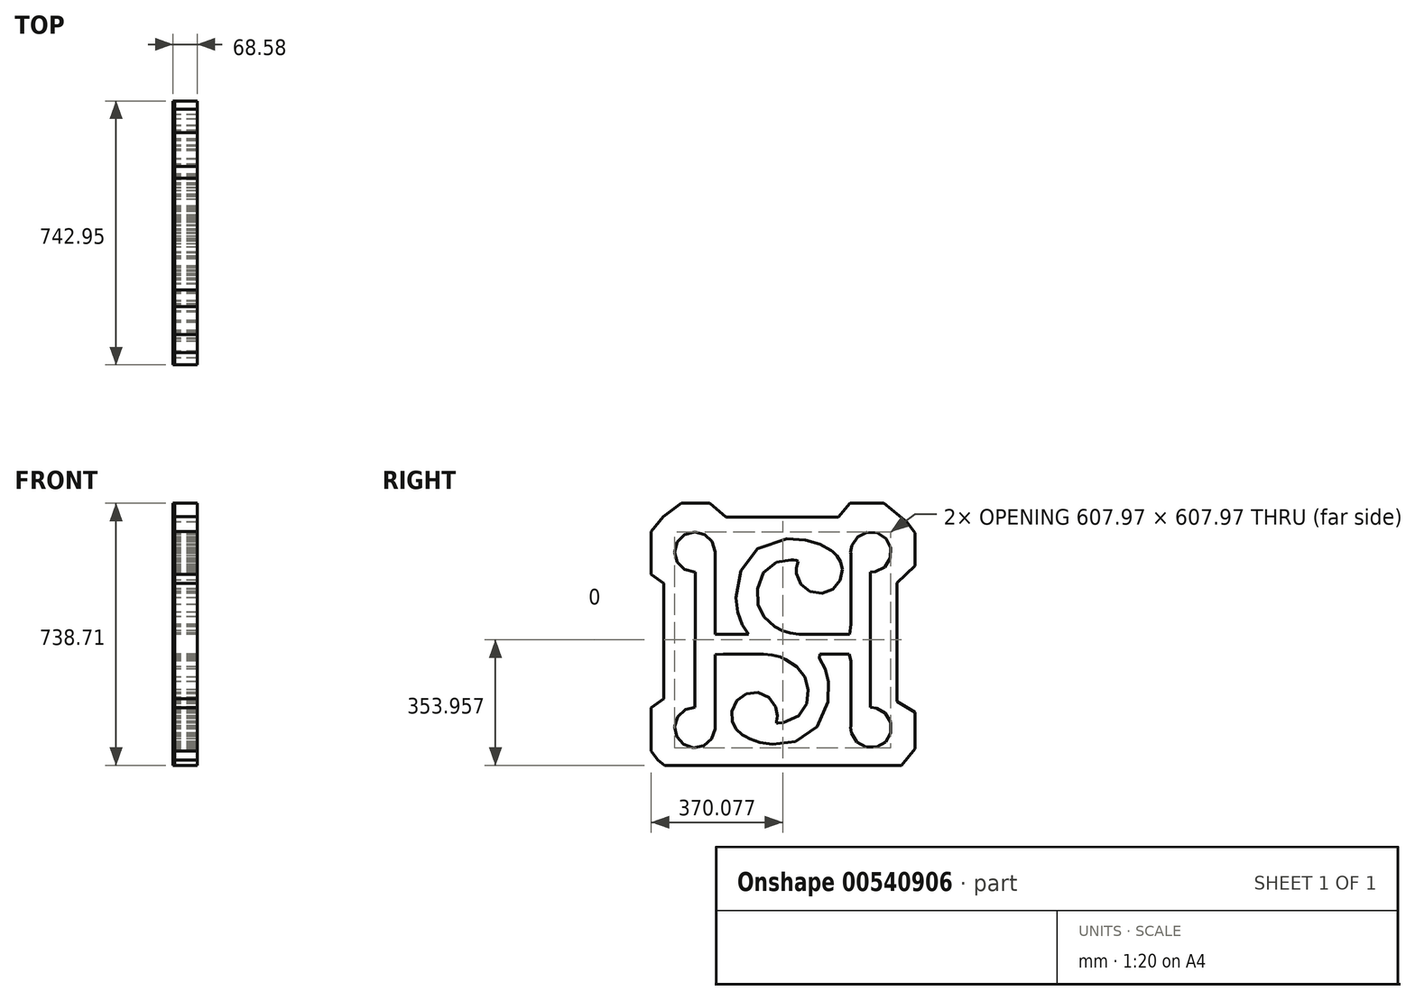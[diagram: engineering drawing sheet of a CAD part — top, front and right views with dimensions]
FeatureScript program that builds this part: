
annotation { "Feature Type Name" : "Feature", "Feature Type Description" : "" }
export const myFeature = defineFeature(function(context is Context, id is Id, definition is map)
    precondition{}
    {
        {
            var Q0;
            Q0=qCreatedBy(makeId("Right.planeOp"),FACE);
            var sketch = newSketch(context, id + "F0", { "sketchPlane" : qUnion([Q0])});
            skFitSpline(sketch, "E0.0", {"points": [v(137.92, 349.27) * mm, v(32.64, 349.27) * mm, v(-72.64, 349.27) * mm, v(-177.92, 349.27) * mm]});
            skFitSpline(sketch, "E1.0", {"points": [v(266.41, 388.54) * mm, v(234.68, 388.54) * mm, v(202.94, 388.54) * mm, v(171.2, 388.54) * mm]});
            skFitSpline(sketch, "E2.0", {"points": [v(171.2, 388.54) * mm, v(160.11, 375.45) * mm, v(149.02, 362.36) * mm, v(137.92, 349.27) * mm]});
            skPoint(sketch, "E3", {"position": v(171.2, 388.54) * mm});
            skFitSpline(sketch, "E4.0", {"points": [v(331.9, 335.96) * mm, v(310.07, 353.48) * mm, v(288.24, 371) * mm, v(266.41, 388.54) * mm]});
            skPoint(sketch, "E5", {"position": v(266.41, 388.54) * mm});
            skPoint(sketch, "E6", {"position": v(-177.92, 349.27) * mm});
            skFitSpline(sketch, "E7.0", {"points": [v(-223.7, 388.54) * mm, v(-250.18, 388.54) * mm, v(-276.66, 388.54) * mm, v(-303.14, 388.54) * mm]});
            skFitSpline(sketch, "E8.0", {"points": [v(-177.92, 349.27) * mm, v(-193.18, 362.36) * mm, v(-208.44, 375.45) * mm, v(-223.7, 388.54) * mm]});
            skPoint(sketch, "E9", {"position": v(-223.7, 388.54) * mm});
            skFitSpline(sketch, "E10.0", {"points": [v(-303.14, 388.54) * mm, v(-320.17, 376.06) * mm, v(-337.2, 363.58) * mm, v(-354.23, 351.1) * mm]});
            skPoint(sketch, "E11", {"position": v(-303.14, 388.54) * mm});
            skFitSpline(sketch, "E12.0", {"points": [v(-354.23, 351.1) * mm, v(-365.59, 336.95) * mm, v(-376.95, 322.8) * mm, v(-388.3, 308.67) * mm]});
            skPoint(sketch, "E13", {"position": v(-354.23, 351.1) * mm});
            skPoint(sketch, "E14", {"position": v(-388.3, 308.67) * mm});
            skFitSpline(sketch, "E15.0", {"points": [v(-388.3, 308.67) * mm, v(-388.3, 268.38) * mm, v(-388.3, 228.1) * mm, v(-388.3, 187.81) * mm]});
            skFitSpline(sketch, "E16.0", {"points": [v(-388.3, 187.81) * mm, v(-376.58, 179.64) * mm, v(-364.86, 171.48) * mm, v(-353.14, 163.31) * mm]});
            skPoint(sketch, "E17", {"position": v(-388.3, 187.81) * mm});
            skPoint(sketch, "E18", {"position": v(-353.14, 163.31) * mm});
            skFitSpline(sketch, "E19.0", {"points": [v(-353.14, -162.05) * mm, v(-364.86, -170.48) * mm, v(-376.58, -178.91) * mm, v(-388.3, -187.34) * mm]});
            skPoint(sketch, "E20", {"position": v(-353.14, -162.05) * mm});
            skPoint(sketch, "E21", {"position": v(-388.3, -187.34) * mm});
            skFitSpline(sketch, "E22.0", {"points": [v(-388.3, -309.2) * mm, v(-382, -317.8) * mm, v(-375.68, -326.42) * mm, v(-369.37, -335.03) * mm]});
            skFitSpline(sketch, "E23.0", {"points": [v(-369.37, -335.03) * mm, v(-363.09, -340.08) * mm, v(-356.8, -345.12) * mm, v(-350.52, -350.17) * mm]});
            skPoint(sketch, "E24", {"position": v(-388.3, -309.2) * mm});
            skPoint(sketch, "E25", {"position": v(-369.37, -335.03) * mm});
            skPoint(sketch, "E26", {"position": v(-350.52, -350.17) * mm});
            skFitSpline(sketch, "E27.0", {"points": [v(-350.52, -350.17) * mm, v(-128.1, -350.17) * mm, v(94.33, -350.17) * mm, v(316.75, -350.17) * mm]});
            skFitSpline(sketch, "E28.0", {"points": [v(316.75, -350.17) * mm, v(329.39, -334.44) * mm, v(342.02, -318.7) * mm, v(354.65, -302.98) * mm]});
            skPoint(sketch, "E29", {"position": v(316.75, -350.17) * mm});
            skLineSegment(sketch, "E30", {"start": v(-353.14, -162.05) * mm, "end": v(-388.3, -187.34) * mm});
            skLineSegment(sketch, "E31", {"start": v(-388.3, -187.34) * mm, "end": v(-388.3, -309.2) * mm});
            skLineSegment(sketch, "E32", {"start": v(-388.3, -309.2) * mm, "end": v(-369.37, -335.03) * mm});
            skLineSegment(sketch, "E33", {"start": v(-369.37, -335.03) * mm, "end": v(-350.52, -350.17) * mm});
            skLineSegment(sketch, "E34", {"start": v(-350.52, -350.17) * mm, "end": v(316.75, -350.17) * mm});
            skLineSegment(sketch, "E35", {"start": v(316.75, -350.17) * mm, "end": v(354.65, -302.98) * mm});
            skLineSegment(sketch, "E36", {"start": v(-353.14, 163.31) * mm, "end": v(-353.14, -162.05) * mm});
            skFitSpline(sketch, "E37.0", {"points": [v(354.65, 304.9) * mm, v(347.06, 315.26) * mm, v(339.48, 325.6) * mm, v(331.9, 335.96) * mm]});
            skFitSpline(sketch, "E38.0", {"points": [v(354.65, 211.87) * mm, v(354.65, 242.88) * mm, v(354.65, 273.9) * mm, v(354.65, 304.9) * mm]});
            skPoint(sketch, "E39", {"position": v(354.65, 304.9) * mm});
            skPoint(sketch, "E40", {"position": v(331.9, 335.96) * mm});
            skFitSpline(sketch, "E41.0", {"points": [v(303.55, 164.27) * mm, v(320.58, 180.14) * mm, v(337.62, 196) * mm, v(354.65, 211.87) * mm]});
            skPoint(sketch, "E42", {"position": v(354.65, 211.87) * mm});
            skFitSpline(sketch, "E43.0", {"points": [v(303.55, -170.62) * mm, v(303.55, -58.99) * mm, v(303.55, 52.64) * mm, v(303.55, 164.27) * mm]});
            skPoint(sketch, "E44", {"position": v(303.55, 164.27) * mm});
            skLineSegment(sketch, "E45", {"start": v(303.55, 164.27) * mm, "end": v(354.65, 211.87) * mm});
            skLineSegment(sketch, "E46", {"start": v(354.65, 211.87) * mm, "end": v(354.65, 304.9) * mm});
            skLineSegment(sketch, "E47", {"start": v(354.65, 304.9) * mm, "end": v(331.9, 335.96) * mm});
            skLineSegment(sketch, "E48", {"start": v(331.9, 335.96) * mm, "end": v(266.41, 388.54) * mm});
            skFitSpline(sketch, "E49.0", {"points": [v(354.65, -200.14) * mm, v(337.62, -190.3) * mm, v(320.58, -180.46) * mm, v(303.55, -170.62) * mm]});
            skFitSpline(sketch, "E50.0", {"points": [v(354.65, -302.98) * mm, v(354.65, -268.7) * mm, v(354.65, -234.42) * mm, v(354.65, -200.14) * mm]});
            skPoint(sketch, "E51", {"position": v(303.55, -170.62) * mm});
            skPoint(sketch, "E52", {"position": v(354.65, -200.14) * mm});
            skPoint(sketch, "E53", {"position": v(354.65, -302.98) * mm});
            skLineSegment(sketch, "E54", {"start": v(303.55, -170.62) * mm, "end": v(354.65, -200.14) * mm});
            skLineSegment(sketch, "E55", {"start": v(354.65, -200.14) * mm, "end": v(354.65, -302.98) * mm});
            skLineSegment(sketch, "E56", {"start": v(355.44, -302.66) * mm, "end": v(316.75, -350.17) * mm});
            skFitSpline(sketch, "E57.0", {"points": [v(-314.53, 279.45) * mm, v(-307.8, 286.25) * mm, v(-301.07, 293.04) * mm, v(-294.34, 299.83) * mm]});
            skPoint(sketch, "E58.0", {"position": v(-265.9, 307.77) * mm});
            skFitSpline(sketch, "E59.0", {"points": [v(-294.34, 299.83) * mm, v(-284.86, 302.48) * mm, v(-275.38, 305.13) * mm, v(-265.9, 307.77) * mm]});
            skPoint(sketch, "E60.0", {"position": v(-322.2, 250.9) * mm});
            skPoint(sketch, "E61.0", {"position": v(-314.53, 222.34) * mm});
            skPoint(sketch, "E62.0", {"position": v(-294.34, 201.96) * mm});
            skPoint(sketch, "E63.0", {"position": v(-237.23, 300.37) * mm});
            skFitSpline(sketch, "E64.0.1", {"points": [v(-294.34, 299.83) * mm, v(-301.07, 293.04) * mm, v(-307.8, 286.25) * mm, v(-314.53, 279.45) * mm]});
            skFitSpline(sketch, "E64.0.2", {"points": [v(-314.53, 279.45) * mm, v(-307.8, 286.25) * mm, v(-301.07, 293.04) * mm, v(-294.34, 299.83) * mm]});
            skFitSpline(sketch, "E65.0.1", {"points": [v(-294.34, 299.83) * mm, v(-284.86, 302.48) * mm, v(-275.38, 305.13) * mm, v(-265.9, 307.77) * mm]});
            skPoint(sketch, "E66", {"position": v(-294.34, 299.83) * mm});
            skPoint(sketch, "E67", {"position": v(-314.53, 279.45) * mm});
            skLineSegment(sketch, "E68", {"start": v(-314.53, 279.45) * mm, "end": v(-322.2, 250.9) * mm});
            skLineSegment(sketch, "E69", {"start": v(-322.2, 250.9) * mm, "end": v(-314.53, 222.34) * mm});
            skLineSegment(sketch, "E70", {"start": v(-314.53, 222.34) * mm, "end": v(-294.34, 201.96) * mm});
            skFitSpline(sketch, "E71.0", {"points": [v(-265.9, 194.01) * mm, v(-275.38, 196.66) * mm, v(-284.86, 199.31) * mm, v(-294.34, 201.96) * mm]});
            skFitSpline(sketch, "E72.0", {"points": [v(-264.88, 194.01) * mm, v(-265.22, 194.01) * mm, v(-265.56, 194.01) * mm, v(-265.9, 194.01) * mm]});
            skPoint(sketch, "E73", {"position": v(-265.9, 194.01) * mm});
            skFitSpline(sketch, "E74.0", {"points": [v(-264.44, 194.02) * mm, v(-264.59, 194.01) * mm, v(-264.73, 194.01) * mm, v(-264.88, 194.01) * mm]});
            skFitSpline(sketch, "E75.0", {"points": [v(-263.99, 194.03) * mm, v(-264.14, 194.03) * mm, v(-264.29, 194.02) * mm, v(-264.44, 194.02) * mm]});
            skPoint(sketch, "E76", {"position": v(-264.88, 194.01) * mm});
            skPoint(sketch, "E77", {"position": v(-264.44, 194.02) * mm});
            skPoint(sketch, "E78", {"position": v(-263.99, 194.03) * mm});
            skLineSegment(sketch, "E79", {"start": v(-263.99, 194.03) * mm, "end": v(-264.44, 194.02) * mm});
            skLineSegment(sketch, "E80", {"start": v(-264.46, 194.02) * mm, "end": v(-264.88, 194.01) * mm});
            skLineSegment(sketch, "E81", {"start": v(-264.88, 194.01) * mm, "end": v(-265.9, 194.01) * mm});
            skFitSpline(sketch, "E82.0", {"points": [v(-208.32, 86.29) * mm, v(-208.32, 64.04) * mm, v(-208.32, 41.8) * mm, v(-208.32, 19.55) * mm]});
            skFitSpline(sketch, "E83.0", {"points": [v(-208.32, 19.55) * mm, v(-201.3, 19.42) * mm, v(-194.29, 19.28) * mm, v(-187.27, 19.14) * mm]});
            skPoint(sketch, "E84", {"position": v(-208.32, 19.55) * mm});
            skPoint(sketch, "E85", {"position": v(-187.27, 19.14) * mm});
            skFitSpline(sketch, "E86.0", {"points": [v(-187.27, 19.14) * mm, v(-172.36, 19.14) * mm, v(-157.45, 19.14) * mm, v(-142.54, 19.14) * mm]});
            skFitSpline(sketch, "E87.0", {"points": [v(-142.54, 19.14) * mm, v(-133.3, 19.14) * mm, v(-124.07, 19.14) * mm, v(-114.84, 19.14) * mm]});
            skPoint(sketch, "E88", {"position": v(-142.54, 19.14) * mm});
            skPoint(sketch, "E89", {"position": v(-114.84, 19.14) * mm});
            skFitSpline(sketch, "E90.0", {"points": [v(-208.32, 250.9) * mm, v(-208.32, 232.94) * mm, v(-208.32, 214.98) * mm, v(-208.32, 197.03) * mm]});
            skPoint(sketch, "E91", {"position": v(-208.32, 250.9) * mm});
            skPoint(sketch, "E92", {"position": v(-208.32, 197.03) * mm});
            skLineSegment(sketch, "E93", {"start": v(-208.32, 250.9) * mm, "end": v(-208.32, 197.03) * mm});
            skLineSegment(sketch, "E94", {"start": v(-208.32, 197.03) * mm, "end": v(-208.32, 86.29) * mm});
            skLineSegment(sketch, "E95", {"start": v(-208.32, 86.29) * mm, "end": v(-208.32, 19.55) * mm});
            skLineSegment(sketch, "E96", {"start": v(-265.9, 307.77) * mm, "end": v(-237.23, 300.37) * mm});
            skFitSpline(sketch, "E97.0", {"points": [v(-237.23, 300.37) * mm, v(-230.38, 293.7) * mm, v(-223.52, 287.04) * mm, v(-216.66, 280.38) * mm]});
            skFitSpline(sketch, "E98.0", {"points": [v(-216.66, 280.38) * mm, v(-213.93, 270.94) * mm, v(-211.19, 261.5) * mm, v(-208.45, 252.05) * mm]});
            skPoint(sketch, "E99", {"position": v(-216.66, 280.38) * mm});
            skLineSegment(sketch, "E100", {"start": v(-237.23, 300.37) * mm, "end": v(-216.66, 280.38) * mm});
            skLineSegment(sketch, "E101", {"start": v(-216.66, 280.38) * mm, "end": v(-208.45, 252.05) * mm});
            skPoint(sketch, "E102", {"position": v(-265.29, -186.54) * mm});
            skFitSpline(sketch, "E103.0", {"points": [v(-291.99, -193.16) * mm, v(-283.09, -190.95) * mm, v(-274.19, -188.74) * mm, v(-265.29, -186.54) * mm]});
            skFitSpline(sketch, "E104.0", {"points": [v(-313.12, -212.56) * mm, v(-306.07, -206.1) * mm, v(-299.03, -199.63) * mm, v(-291.99, -193.16) * mm]});
            skPoint(sketch, "E105", {"position": v(-291.99, -193.16) * mm});
            skFitSpline(sketch, "E106.0", {"points": [v(-322.13, -240.54) * mm, v(-319.13, -231.22) * mm, v(-316.12, -221.9) * mm, v(-313.12, -212.56) * mm]});
            skFitSpline(sketch, "E107.0", {"points": [v(-315.83, -269.6) * mm, v(-317.93, -259.92) * mm, v(-320.03, -250.23) * mm, v(-322.13, -240.54) * mm]});
            skPoint(sketch, "E108", {"position": v(-322.13, -240.54) * mm});
            skPoint(sketch, "E109", {"position": v(-315.83, -269.6) * mm});
            skFitSpline(sketch, "E110.0", {"points": [v(-296.62, -290.92) * mm, v(-303.02, -283.81) * mm, v(-309.43, -276.7) * mm, v(-315.83, -269.6) * mm]});
            skFitSpline(sketch, "E111.0", {"points": [v(-268.77, -300.2) * mm, v(-278.05, -297.1) * mm, v(-287.33, -294.01) * mm, v(-296.62, -290.92) * mm]});
            skPoint(sketch, "E112", {"position": v(-296.62, -290.92) * mm});
            skPoint(sketch, "E113", {"position": v(-268.77, -300.2) * mm});
            skFitSpline(sketch, "E114.0", {"points": [v(-239.61, -294.17) * mm, v(-249.33, -296.18) * mm, v(-259.05, -298.2) * mm, v(-268.77, -300.2) * mm]});
            skFitSpline(sketch, "E115.0", {"points": [v(-218.11, -275.16) * mm, v(-225.28, -281.5) * mm, v(-232.45, -287.84) * mm, v(-239.61, -294.17) * mm]});
            skFitSpline(sketch, "E116.0", {"points": [v(-208.58, -247.43) * mm, v(-211.76, -256.67) * mm, v(-214.94, -265.92) * mm, v(-218.11, -275.16) * mm]});
            skPoint(sketch, "E117", {"position": v(-239.61, -294.17) * mm});
            skPoint(sketch, "E118", {"position": v(-218.11, -275.16) * mm});
            skPoint(sketch, "E119", {"position": v(-208.58, -247.43) * mm});
            skLineSegment(sketch, "E120", {"start": v(-265.29, -186.54) * mm, "end": v(-291.99, -193.16) * mm});
            skLineSegment(sketch, "E121", {"start": v(-291.99, -193.16) * mm, "end": v(-313.12, -212.56) * mm});
            skLineSegment(sketch, "E122", {"start": v(-313.12, -212.56) * mm, "end": v(-322.13, -240.54) * mm});
            skLineSegment(sketch, "E123", {"start": v(-322.13, -240.54) * mm, "end": v(-315.83, -269.6) * mm});
            skLineSegment(sketch, "E124", {"start": v(-315.83, -269.6) * mm, "end": v(-296.62, -290.92) * mm});
            skLineSegment(sketch, "E125", {"start": v(-296.62, -290.92) * mm, "end": v(-268.77, -300.2) * mm});
            skLineSegment(sketch, "E126", {"start": v(-268.77, -300.2) * mm, "end": v(-239.61, -294.17) * mm});
            skLineSegment(sketch, "E127", {"start": v(-239.61, -294.17) * mm, "end": v(-218.11, -275.16) * mm});
            skLineSegment(sketch, "E128", {"start": v(-218.11, -275.16) * mm, "end": v(-208.58, -247.43) * mm});
            skFitSpline(sketch, "E129.0", {"points": [v(-185.5, -36.6) * mm, v(-193.11, -37.21) * mm, v(-200.72, -37.82) * mm, v(-208.32, -38.43) * mm]});
            skFitSpline(sketch, "E130.0", {"points": [v(-208.32, -105.4) * mm, v(-208.32, -138.04) * mm, v(-208.32, -170.67) * mm, v(-208.32, -203.3) * mm]});
            skFitSpline(sketch, "E131.0", {"points": [v(-208.32, -38.43) * mm, v(-208.32, -60.75) * mm, v(-208.32, -83.08) * mm, v(-208.32, -105.4) * mm]});
            skPoint(sketch, "E132", {"position": v(-208.32, -105.4) * mm});
            skPoint(sketch, "E133", {"position": v(-208.32, -203.3) * mm});
            skPoint(sketch, "E134", {"position": v(-208.32, -38.43) * mm});
            skPoint(sketch, "E135", {"position": v(-185.5, -36.6) * mm});
            skFitSpline(sketch, "E136.0", {"points": [v(-124.56, -36.6) * mm, v(-144.88, -36.6) * mm, v(-165.2, -36.6) * mm, v(-185.5, -36.6) * mm]});
            skFitSpline(sketch, "E137.0", {"points": [v(-71.96, -36.6) * mm, v(-89.5, -36.6) * mm, v(-107.03, -36.6) * mm, v(-124.56, -36.6) * mm]});
            skPoint(sketch, "E138", {"position": v(-124.56, -36.6) * mm});
            skPoint(sketch, "E139", {"position": v(-71.96, -36.6) * mm});
            skFitSpline(sketch, "E140.0", {"points": [v(-48.35, -38.7) * mm, v(-56.22, -38) * mm, v(-64.09, -37.3) * mm, v(-71.96, -36.6) * mm]});
            skFitSpline(sketch, "E141.0", {"points": [v(-25.85, -44.9) * mm, v(-33.35, -42.83) * mm, v(-40.85, -40.77) * mm, v(-48.35, -38.7) * mm]});
            skFitSpline(sketch, "E142.0", {"points": [v(-9.64, -51.5) * mm, v(-15.04, -49.3) * mm, v(-20.45, -47.1) * mm, v(-25.85, -44.9) * mm]});
            skFitSpline(sketch, "E143.0", {"points": [v(21.14, -72.52) * mm, v(10.88, -65.52) * mm, v(0.62, -58.51) * mm, v(-9.64, -51.5) * mm]});
            skFitSpline(sketch, "E144.0", {"points": [v(44.2, -101.08) * mm, v(36.52, -91.56) * mm, v(28.83, -82.04) * mm, v(21.14, -72.52) * mm]});
            skPoint(sketch, "E145", {"position": v(-48.35, -38.7) * mm});
            skPoint(sketch, "E146", {"position": v(-25.85, -44.9) * mm});
            skPoint(sketch, "E147", {"position": v(-9.64, -51.5) * mm});
            skPoint(sketch, "E148", {"position": v(21.14, -72.52) * mm});
            skFitSpline(sketch, "E149.0", {"points": [v(26.65, -211.2) * mm, v(34.1, -199.72) * mm, v(41.53, -188.24) * mm, v(48.97, -176.76) * mm]});
            skPoint(sketch, "E150", {"position": v(44.2, -101.08) * mm});
            skFitSpline(sketch, "E151.0", {"points": [v(53.55, -137.12) * mm, v(50.44, -125.1) * mm, v(47.32, -113.09) * mm, v(44.2, -101.08) * mm]});
            skPoint(sketch, "E152", {"position": v(53.55, -137.12) * mm});
            skPoint(sketch, "E153", {"position": v(48.97, -176.76) * mm});
            skLineSegment(sketch, "E154", {"start": v(53.55, -137.12) * mm, "end": v(48.97, -176.76) * mm});
            skFitSpline(sketch, "E155.0", {"points": [v(129.27, -36.6) * mm, v(115.07, -36.6) * mm, v(100.87, -36.6) * mm, v(86.68, -36.6) * mm]});
            skFitSpline(sketch, "E156.0", {"points": [v(168.35, -36.6) * mm, v(155.32, -36.6) * mm, v(142.3, -36.6) * mm, v(129.27, -36.6) * mm]});
            skFitSpline(sketch, "E157.0", {"points": [v(86.68, -36.6) * mm, v(86.33, -40.32) * mm, v(85.98, -44.03) * mm, v(85.62, -47.75) * mm]});
            skFitSpline(sketch, "E158.0", {"points": [v(85.62, -47.75) * mm, v(91.07, -57.93) * mm, v(96.5, -68.1) * mm, v(101.95, -78.29) * mm]});
            skFitSpline(sketch, "E159.0", {"points": [v(101.95, -78.29) * mm, v(104.92, -90.13) * mm, v(107.88, -101.97) * mm, v(110.84, -113.8) * mm]});
            skLineSegment(sketch, "E160", {"start": v(86.68, -36.6) * mm, "end": v(129.27, -36.6) * mm});
            skLineSegment(sketch, "E161", {"start": v(129.27, -36.6) * mm, "end": v(168.35, -36.6) * mm});
            skLineSegment(sketch, "E162", {"start": v(101.95, -78.29) * mm, "end": v(110.84, -113.8) * mm});
            skFitSpline(sketch, "E163.0", {"points": [v(109.56, -170.81) * mm, v(99.18, -194.07) * mm, v(88.8, -217.33) * mm, v(78.42, -240.59) * mm]});
            skFitSpline(sketch, "E164.0", {"points": [v(110.84, -113.8) * mm, v(110.42, -132.8) * mm, v(109.99, -151.8) * mm, v(109.56, -170.81) * mm]});
            skLineSegment(sketch, "E165", {"start": v(110.84, -113.8) * mm, "end": v(109.56, -170.81) * mm});
            skLineSegment(sketch, "E166", {"start": v(109.56, -170.81) * mm, "end": v(78.42, -240.59) * mm});
            skFitSpline(sketch, "E167.0", {"points": [v(-16.67, -229.9) * mm, v(-2.23, -223.66) * mm, v(12.21, -217.43) * mm, v(26.65, -211.2) * mm]});
            skFitSpline(sketch, "E168.0", {"points": [v(-32.15, -230.73) * mm, v(-26.99, -230.45) * mm, v(-21.83, -230.17) * mm, v(-16.67, -229.9) * mm]});
            skLineSegment(sketch, "E169", {"start": v(26.65, -211.2) * mm, "end": v(-16.67, -229.9) * mm});
            skLineSegment(sketch, "E170", {"start": v(48.97, -176.76) * mm, "end": v(26.65, -211.2) * mm});
            skFitSpline(sketch, "E171.0", {"points": [v(-34.19, -230.7) * mm, v(-33.5, -230.7) * mm, v(-32.83, -230.72) * mm, v(-32.15, -230.73) * mm]});
            skFitSpline(sketch, "E172.0", {"points": [v(-34.19, -230.7) * mm, v(-34.86, -230.67) * mm, v(-35.53, -230.64) * mm, v(-36.2, -230.62) * mm]});
            skFitSpline(sketch, "E173.0", {"points": [v(-35.18, -225.55) * mm, v(-34.7, -223.2) * mm, v(-34.21, -220.83) * mm, v(-33.73, -218.47) * mm]});
            skFitSpline(sketch, "E174.0", {"points": [v(-33.08, -211.13) * mm, v(-33.3, -213.58) * mm, v(-33.52, -216.03) * mm, v(-33.73, -218.47) * mm]});
            skPoint(sketch, "E175", {"position": v(-32.15, -230.73) * mm});
            skPoint(sketch, "E176", {"position": v(-34.19, -230.7) * mm});
            skPoint(sketch, "E177", {"position": v(-36.2, -230.62) * mm});
            skPoint(sketch, "E178", {"position": v(-35.18, -225.55) * mm});
            skPoint(sketch, "E179", {"position": v(-33.73, -218.47) * mm});
            skPoint(sketch, "E180", {"position": v(-16.67, -229.9) * mm});
            skLineSegment(sketch, "E181", {"start": v(-16.67, -229.9) * mm, "end": v(-32.15, -230.73) * mm});
            skLineSegment(sketch, "E182", {"start": v(-32.15, -230.73) * mm, "end": v(-34.19, -230.7) * mm});
            skLineSegment(sketch, "E183", {"start": v(-34.19, -230.7) * mm, "end": v(-36.2, -230.62) * mm});
            skLineSegment(sketch, "E184", {"start": v(-36.2, -230.62) * mm, "end": v(-35.18, -225.55) * mm});
            skLineSegment(sketch, "E185", {"start": v(-35.18, -225.55) * mm, "end": v(-33.73, -218.47) * mm});
            skFitSpline(sketch, "E186.0", {"points": [v(-57.2, -158.66) * mm, v(-50.7, -167.4) * mm, v(-44.21, -176.15) * mm, v(-37.72, -184.9) * mm]});
            skFitSpline(sketch, "E187.0", {"points": [v(-87.4, -145.21) * mm, v(-77.34, -149.7) * mm, v(-67.27, -154.18) * mm, v(-57.2, -158.66) * mm]});
            skFitSpline(sketch, "E188.0", {"points": [v(-37.72, -184.9) * mm, v(-36.17, -193.64) * mm, v(-34.63, -202.39) * mm, v(-33.08, -211.13) * mm]});
            skPoint(sketch, "E189", {"position": v(-57.2, -158.66) * mm});
            skPoint(sketch, "E190", {"position": v(-37.72, -184.9) * mm});
            skPoint(sketch, "E191", {"position": v(-33.08, -211.13) * mm});
            skLineSegment(sketch, "E192", {"start": v(-33.08, -211.13) * mm, "end": v(-37.72, -184.9) * mm});
            skLineSegment(sketch, "E193", {"start": v(-37.72, -184.9) * mm, "end": v(-57.2, -158.66) * mm});
            skLineSegment(sketch, "E194", {"start": v(-33.08, -211.13) * mm, "end": v(-33.73, -218.47) * mm});
            skFitSpline(sketch, "E195.0", {"points": [v(-121.3, -148.84) * mm, v(-110, -147.63) * mm, v(-98.7, -146.42) * mm, v(-87.4, -145.21) * mm]});
            skFitSpline(sketch, "E196.0", {"points": [v(-147.72, -168.08) * mm, v(-138.92, -161.66) * mm, v(-130.1, -155.25) * mm, v(-121.3, -148.84) * mm]});
            skFitSpline(sketch, "E197.0", {"points": [v(-161.45, -198.13) * mm, v(-156.87, -188.11) * mm, v(-152.3, -178.1) * mm, v(-147.72, -168.08) * mm]});
            skPoint(sketch, "E198", {"position": v(-121.3, -148.84) * mm});
            skPoint(sketch, "E199", {"position": v(-87.4, -145.21) * mm});
            skPoint(sketch, "E200", {"position": v(-147.72, -168.08) * mm});
            skLineSegment(sketch, "E201", {"start": v(-57.2, -158.66) * mm, "end": v(-87.4, -145.21) * mm});
            skLineSegment(sketch, "E202", {"start": v(-87.4, -145.21) * mm, "end": v(-121.3, -148.84) * mm});
            skLineSegment(sketch, "E203", {"start": v(-121.3, -148.84) * mm, "end": v(-147.72, -168.08) * mm});
            skLineSegment(sketch, "E204", {"start": v(-147.72, -168.08) * mm, "end": v(-161.45, -198.13) * mm});
            skFitSpline(sketch, "E205.0", {"points": [v(-160.08, -226.14) * mm, v(-160.54, -216.8) * mm, v(-161, -207.46) * mm, v(-161.45, -198.13) * mm]});
            skFitSpline(sketch, "E206.0", {"points": [v(-149.46, -247.82) * mm, v(-153, -240.6) * mm, v(-156.54, -233.36) * mm, v(-160.08, -226.14) * mm]});
            skFitSpline(sketch, "E207.0", {"points": [v(-131.86, -263.96) * mm, v(-137.73, -258.58) * mm, v(-143.6, -253.2) * mm, v(-149.46, -247.82) * mm]});
            skFitSpline(sketch, "E208.0", {"points": [v(-124.76, -267.8) * mm, v(-127.13, -266.53) * mm, v(-129.5, -265.24) * mm, v(-131.86, -263.96) * mm]});
            skFitSpline(sketch, "E209.0", {"points": [v(-110.14, -275.44) * mm, v(-115, -272.9) * mm, v(-119.86, -270.37) * mm, v(-124.71, -267.83) * mm]});
            skFitSpline(sketch, "E210.0", {"points": [v(-82.04, -285.03) * mm, v(-91.4, -281.83) * mm, v(-100.77, -278.64) * mm, v(-110.14, -275.44) * mm]});
            skFitSpline(sketch, "E211.0", {"points": [v(-47.18, -290.29) * mm, v(-58.8, -288.54) * mm, v(-70.42, -286.78) * mm, v(-82.04, -285.03) * mm]});
            skPoint(sketch, "E212", {"position": v(-161.45, -198.13) * mm});
            skPoint(sketch, "E213", {"position": v(-160.08, -226.14) * mm});
            skPoint(sketch, "E214", {"position": v(-149.46, -247.82) * mm});
            skPoint(sketch, "E215", {"position": v(-131.86, -263.96) * mm});
            skPoint(sketch, "E216", {"position": v(-124.71, -267.83) * mm});
            skPoint(sketch, "E217", {"position": v(-110.14, -275.44) * mm});
            skPoint(sketch, "E218", {"position": v(-82.04, -285.03) * mm});
            skPoint(sketch, "E219", {"position": v(-47.18, -290.29) * mm});
            skLineSegment(sketch, "E220", {"start": v(-161.54, -198.14) * mm, "end": v(-160.08, -226.14) * mm});
            skLineSegment(sketch, "E221", {"start": v(-160.08, -226.14) * mm, "end": v(-149.46, -247.82) * mm});
            skLineSegment(sketch, "E222", {"start": v(-149.46, -247.82) * mm, "end": v(-131.86, -263.96) * mm});
            skLineSegment(sketch, "E223", {"start": v(-131.86, -263.96) * mm, "end": v(-124.71, -267.83) * mm});
            skLineSegment(sketch, "E224", {"start": v(-124.71, -267.83) * mm, "end": v(-110.14, -275.44) * mm});
            skLineSegment(sketch, "E225", {"start": v(-110.14, -275.44) * mm, "end": v(-82.04, -285.03) * mm});
            skLineSegment(sketch, "E226", {"start": v(-82.04, -285.03) * mm, "end": v(-47.18, -290.29) * mm});
            skFitSpline(sketch, "E227.0", {"points": [v(17.85, -282.65) * mm, v(-3.83, -285.2) * mm, v(-25.5, -287.74) * mm, v(-47.18, -290.29) * mm]});
            skFitSpline(sketch, "E228.0", {"points": [v(78.42, -240.59) * mm, v(58.23, -254.6) * mm, v(38.04, -268.63) * mm, v(17.85, -282.65) * mm]});
            skPoint(sketch, "E229", {"position": v(17.85, -282.65) * mm});
            skLineSegment(sketch, "E230", {"start": v(-47.18, -290.29) * mm, "end": v(17.85, -282.65) * mm});
            skLineSegment(sketch, "E231", {"start": v(17.85, -282.65) * mm, "end": v(78.42, -240.59) * mm});
            skFitSpline(sketch, "E232.0", {"points": [v(190.57, -284.2) * mm, v(185.6, -275.97) * mm, v(180.62, -267.74) * mm, v(175.65, -259.5) * mm]});
            skFitSpline(sketch, "E233.0", {"points": [v(215.72, -298.44) * mm, v(207.33, -293.7) * mm, v(198.95, -288.95) * mm, v(190.57, -284.2) * mm]});
            skFitSpline(sketch, "E234.0", {"points": [v(245.78, -298.15) * mm, v(235.76, -298.24) * mm, v(225.74, -298.34) * mm, v(215.72, -298.44) * mm]});
            skFitSpline(sketch, "E235.0", {"points": [v(175.65, -259.5) * mm, v(174.88, -253.88) * mm, v(174.11, -248.25) * mm, v(173.34, -242.62) * mm]});
            skFitSpline(sketch, "E236.0", {"points": [v(270.63, -203.38) * mm, v(275.45, -211.72) * mm, v(280.27, -220.05) * mm, v(285.1, -228.38) * mm]});
            skFitSpline(sketch, "E237.0", {"points": [v(245.78, -188.7) * mm, v(254.06, -193.59) * mm, v(262.35, -198.49) * mm, v(270.63, -203.38) * mm]});
            skFitSpline(sketch, "E238.0", {"points": [v(229.87, -186.54) * mm, v(235.17, -187.26) * mm, v(240.48, -187.97) * mm, v(245.78, -188.7) * mm]});
            skFitSpline(sketch, "E239.0", {"points": [v(229.15, -186.55) * mm, v(229.4, -186.55) * mm, v(229.63, -186.54) * mm, v(229.87, -186.54) * mm]});
            skFitSpline(sketch, "E240.0", {"points": [v(228.43, -186.57) * mm, v(228.67, -186.56) * mm, v(228.91, -186.56) * mm, v(229.15, -186.55) * mm]});
            skPoint(sketch, "E241", {"position": v(228.43, -186.57) * mm});
            skPoint(sketch, "E242", {"position": v(229.15, -186.55) * mm});
            skPoint(sketch, "E243", {"position": v(229.87, -186.54) * mm});
            skLineSegment(sketch, "E244", {"start": v(228.43, -186.57) * mm, "end": v(229.15, -186.55) * mm});
            skLineSegment(sketch, "E245", {"start": v(229.16, -186.54) * mm, "end": v(229.87, -186.54) * mm});
            skLineSegment(sketch, "E246", {"start": v(285.1, -228.38) * mm, "end": v(285.1, -258.45) * mm});
            skPoint(sketch, "E247", {"position": v(271.3, -283.77) * mm});
            skPoint(sketch, "E248.0.end.orphan", {"position": v(285.1, -258.45) * mm});
            skPoint(sketch, "E248.0.start.orphan", {"position": v(285.76, 263.24) * mm});
            skFitSpline(sketch, "E249.0.0", {"points": [v(123.52, 19.14) * mm, v(103.07, 19.14) * mm, v(82.62, 19.14) * mm, v(62.17, 19.14) * mm]});
            skFitSpline(sketch, "E249.0.2", {"points": [v(62.17, 19.14) * mm, v(82.62, 19.14) * mm, v(103.07, 19.14) * mm, v(123.52, 19.14) * mm]});
            skFitSpline(sketch, "E250.0", {"points": [v(28, 19.44) * mm, v(39.4, 19.34) * mm, v(50.78, 19.24) * mm, v(62.17, 19.14) * mm]});
            skFitSpline(sketch, "E251.0", {"points": [v(123.52, 19.14) * mm, v(138.88, 19.14) * mm, v(154.24, 19.14) * mm, v(169.6, 19.14) * mm]});
            skPoint(sketch, "E252", {"position": v(62.17, 19.14) * mm});
            skPoint(sketch, "E253", {"position": v(123.52, 19.14) * mm});
            skPoint(sketch, "E254", {"position": v(28, 19.44) * mm});
            skLineSegment(sketch, "E255", {"start": v(28, 19.44) * mm, "end": v(62.17, 19.14) * mm});
            skLineSegment(sketch, "E256", {"start": v(62.17, 19.14) * mm, "end": v(123.52, 19.14) * mm});
            skFitSpline(sketch, "E257.0", {"points": [v(2.84, 23.3) * mm, v(11.23, 22.02) * mm, v(19.62, 20.73) * mm, v(28, 19.44) * mm]});
            skFitSpline(sketch, "E258.0", {"points": [v(-19.1, 29.1) * mm, v(-11.78, 27.16) * mm, v(-4.47, 25.23) * mm, v(2.84, 23.3) * mm]});
            skPoint(sketch, "E259", {"position": v(2.84, 23.3) * mm});
            skFitSpline(sketch, "E260.0", {"points": [v(-40.14, 40.25) * mm, v(-33.13, 36.53) * mm, v(-26.1, 32.81) * mm, v(-19.1, 29.1) * mm]});
            skPoint(sketch, "E261", {"position": v(-19.1, 29.1) * mm});
            skFitSpline(sketch, "E262.0", {"points": [v(-71.2, 68.55) * mm, v(-60.85, 59.12) * mm, v(-50.5, 49.69) * mm, v(-40.14, 40.25) * mm]});
            skPoint(sketch, "E263", {"position": v(-40.14, 40.25) * mm});
            skLineSegment(sketch, "E264", {"start": v(-40.14, 40.25) * mm, "end": v(-19.1, 29.1) * mm});
            skLineSegment(sketch, "E265", {"start": v(-19.1, 29.1) * mm, "end": v(2.84, 23.3) * mm});
            skLineSegment(sketch, "E266", {"start": v(2.84, 23.3) * mm, "end": v(28, 19.44) * mm});
            skLineSegment(sketch, "E267", {"start": v(-71.2, 68.55) * mm, "end": v(-40.14, 40.25) * mm});
            skFitSpline(sketch, "E268.0", {"points": [v(-89.56, 147.96) * mm, v(-88.78, 132.87) * mm, v(-88, 117.79) * mm, v(-87.2, 102.7) * mm]});
            skPoint(sketch, "E269", {"position": v(-87.2, 102.7) * mm});
            skLineSegment(sketch, "E270", {"start": v(-87.2, 102.7) * mm, "end": v(-71.2, 68.55) * mm});
            skFitSpline(sketch, "E271.0", {"points": [v(-72.6, 193.7) * mm, v(-78.25, 178.45) * mm, v(-83.9, 163.2) * mm, v(-89.56, 147.96) * mm]});
            skPoint(sketch, "E272", {"position": v(-89.56, 147.96) * mm});
            skLineSegment(sketch, "E273", {"start": v(-89.56, 147.96) * mm, "end": v(-87.2, 102.7) * mm});
            skFitSpline(sketch, "E274.0", {"points": [v(92.09, 134.39) * mm, v(80.9, 136.14) * mm, v(69.7, 137.89) * mm, v(58.51, 139.64) * mm]});
            skFitSpline(sketch, "E275.0", {"points": [v(123.05, 146.4) * mm, v(112.73, 142.4) * mm, v(102.4, 138.4) * mm, v(92.09, 134.39) * mm]});
            skFitSpline(sketch, "E276.0", {"points": [v(58.51, 139.64) * mm, v(50.03, 146.45) * mm, v(41.55, 153.27) * mm, v(33.06, 160.09) * mm]});
            skPoint(sketch, "E277", {"position": v(58.51, 139.64) * mm});
            skPoint(sketch, "E278", {"position": v(92.09, 134.39) * mm});
            skLineSegment(sketch, "E279", {"start": v(92.09, 134.39) * mm, "end": v(58.51, 139.64) * mm});
            skLineSegment(sketch, "E280", {"start": v(123.05, 146.4) * mm, "end": v(92.09, 134.39) * mm});
            skLineSegment(sketch, "E281", {"start": v(58.51, 139.64) * mm, "end": v(33.06, 160.09) * mm});
            skFitSpline(sketch, "E282.0", {"points": [v(143.72, 171.67) * mm, v(136.83, 163.25) * mm, v(129.94, 154.83) * mm, v(123.05, 146.4) * mm]});
            skPoint(sketch, "E283", {"position": v(143.72, 171.67) * mm});
            skPoint(sketch, "E284", {"position": v(123.05, 146.4) * mm});
            skLineSegment(sketch, "E285", {"start": v(123.05, 146.4) * mm, "end": v(143.72, 171.67) * mm});
            skFitSpline(sketch, "E286.0", {"points": [v(144.79, 223.23) * mm, v(146.36, 216.4) * mm, v(147.92, 209.56) * mm, v(149.5, 202.72) * mm]});
            skPoint(sketch, "E287", {"position": v(149.5, 202.72) * mm});
            skLineSegment(sketch, "E288", {"start": v(149.5, 202.72) * mm, "end": v(143.72, 171.67) * mm});
            skFitSpline(sketch, "E289.0", {"points": [v(134.12, 240.66) * mm, v(137.68, 234.85) * mm, v(141.23, 229.04) * mm, v(144.79, 223.23) * mm]});
            skFitSpline(sketch, "E290.0", {"points": [v(118, 255.73) * mm, v(119.22, 254.7) * mm, v(120.44, 253.68) * mm, v(121.66, 252.66) * mm]});
            skFitSpline(sketch, "E291.0", {"points": [v(121.66, 252.66) * mm, v(125.81, 248.66) * mm, v(129.97, 244.66) * mm, v(134.12, 240.66) * mm]});
            skFitSpline(sketch, "E292.0", {"points": [v(85.78, 273.2) * mm, v(96.52, 267.38) * mm, v(107.26, 261.55) * mm, v(118, 255.73) * mm]});
            skPoint(sketch, "E293", {"position": v(118, 255.73) * mm});
            skPoint(sketch, "E294", {"position": v(121.66, 252.66) * mm});
            skPoint(sketch, "E295", {"position": v(134.12, 240.66) * mm});
            skLineSegment(sketch, "E296", {"start": v(134.12, 240.66) * mm, "end": v(121.66, 252.66) * mm});
            skLineSegment(sketch, "E297", {"start": v(121.66, 252.66) * mm, "end": v(118, 255.73) * mm});
            skLineSegment(sketch, "E298", {"start": v(118, 255.73) * mm, "end": v(85.78, 273.2) * mm});
            skFitSpline(sketch, "E299.0", {"points": [v(45.05, 285) * mm, v(58.62, 281.07) * mm, v(72.2, 277.14) * mm, v(85.78, 273.2) * mm]});
            skLineSegment(sketch, "E300", {"start": v(85.78, 273.2) * mm, "end": v(45.05, 285) * mm});
            skFitSpline(sketch, "E301.0", {"points": [v(-6, 288.26) * mm, v(11.01, 287.18) * mm, v(28.03, 286.09) * mm, v(45.05, 285) * mm]});
            skFitSpline(sketch, "E302.0", {"points": [v(-88.65, 260.47) * mm, v(-61.1, 269.73) * mm, v(-33.56, 279) * mm, v(-6, 288.26) * mm]});
            skPoint(sketch, "E303", {"position": v(-6, 288.26) * mm});
            skPoint(sketch, "E304", {"position": v(45.05, 285) * mm});
            skPoint(sketch, "E305", {"position": v(85.78, 273.2) * mm});
            skLineSegment(sketch, "E306", {"start": v(45.05, 285) * mm, "end": v(-6, 288.26) * mm});
            skFitSpline(sketch, "E307.0", {"points": [v(-136.2, 198.88) * mm, v(-120.36, 219.4) * mm, v(-104.5, 239.94) * mm, v(-88.65, 260.47) * mm]});
            skFitSpline(sketch, "E308.0", {"points": [v(-149.57, 121.95) * mm, v(-145.11, 147.6) * mm, v(-140.66, 173.23) * mm, v(-136.2, 198.88) * mm]});
            skFitSpline(sketch, "E309.0", {"points": [v(-144.85, 80.92) * mm, v(-146.42, 94.6) * mm, v(-148, 108.27) * mm, v(-149.57, 121.95) * mm]});
            skLineSegment(sketch, "E310", {"start": v(-88.65, 260.47) * mm, "end": v(-136.2, 198.88) * mm});
            skLineSegment(sketch, "E311", {"start": v(-136.2, 198.88) * mm, "end": v(-149.57, 121.95) * mm});
            skLineSegment(sketch, "E312", {"start": v(-149.57, 121.95) * mm, "end": v(-144.85, 80.92) * mm});
            skFitSpline(sketch, "E313.0", {"points": [v(-132.44, 46.14) * mm, v(-136.58, 57.73) * mm, v(-140.71, 69.33) * mm, v(-144.85, 80.92) * mm]});
            skFitSpline(sketch, "E314.0", {"points": [v(-114.84, 19.14) * mm, v(-120.7, 28.14) * mm, v(-126.58, 37.14) * mm, v(-132.44, 46.14) * mm]});
            skPoint(sketch, "E315", {"position": v(-132.44, 46.14) * mm});
            skPoint(sketch, "E316", {"position": v(-144.85, 80.92) * mm});
            skPoint(sketch, "E317", {"position": v(-149.57, 121.95) * mm});
            skLineSegment(sketch, "E318", {"start": v(-144.85, 80.92) * mm, "end": v(-132.44, 46.14) * mm});
            skPoint(sketch, "E319", {"position": v(-136.2, 198.88) * mm});
            skLineSegment(sketch, "E320", {"start": v(-136, 198.58) * mm, "end": v(-149.57, 121.95) * mm});
            skFitSpline(sketch, "E321.0", {"points": [v(-35.65, 221.88) * mm, v(-47.96, 212.49) * mm, v(-60.28, 203.1) * mm, v(-72.6, 193.7) * mm]});
            skFitSpline(sketch, "E322.0", {"points": [v(5.36, 228.62) * mm, v(-8.3, 226.38) * mm, v(-21.98, 224.13) * mm, v(-35.65, 221.88) * mm]});
            skFitSpline(sketch, "E323.0", {"points": [v(13.16, 228.3) * mm, v(10.56, 228.4) * mm, v(7.96, 228.52) * mm, v(5.36, 228.62) * mm]});
            skFitSpline(sketch, "E324.0", {"points": [v(20.9, 227.57) * mm, v(18.32, 227.81) * mm, v(15.74, 228.06) * mm, v(13.16, 228.3) * mm]});
            skFitSpline(sketch, "E325.0", {"points": [v(20.9, 227.57) * mm, v(22.51, 226.62) * mm, v(24.13, 225.67) * mm, v(25.75, 224.72) * mm]});
            skFitSpline(sketch, "E326.0", {"points": [v(25.75, 224.72) * mm, v(24.7, 221.75) * mm, v(23.64, 218.78) * mm, v(22.6, 215.8) * mm]});
            skFitSpline(sketch, "E327.0", {"points": [v(20.75, 206.35) * mm, v(21.36, 209.5) * mm, v(21.98, 212.65) * mm, v(22.6, 215.8) * mm]});
            skPoint(sketch, "E328", {"position": v(22.6, 215.8) * mm});
            skPoint(sketch, "E329", {"position": v(25.75, 224.72) * mm});
            skPoint(sketch, "E330", {"position": v(20.9, 227.57) * mm});
            skPoint(sketch, "E331", {"position": v(13.16, 228.3) * mm});
            skPoint(sketch, "E332", {"position": v(5.36, 228.62) * mm});
            skLineSegment(sketch, "E333", {"start": v(5.36, 228.62) * mm, "end": v(13.16, 228.3) * mm});
            skLineSegment(sketch, "E334", {"start": v(20.9, 227.57) * mm, "end": v(25.75, 224.72) * mm});
            skLineSegment(sketch, "E335", {"start": v(25.75, 224.72) * mm, "end": v(22.6, 215.8) * mm});
            skFitSpline(sketch, "E336.0", {"points": [v(33.06, 160.09) * mm, v(28.96, 170.36) * mm, v(24.86, 180.64) * mm, v(20.76, 190.9) * mm]});
            skFitSpline(sketch, "E337.0", {"points": [v(20.76, 190.9) * mm, v(20.76, 196.06) * mm, v(20.75, 201.2) * mm, v(20.75, 206.35) * mm]});
            skLineSegment(sketch, "E338", {"start": v(20.76, 190.9) * mm, "end": v(33.06, 160.09) * mm});
            skLineSegment(sketch, "E339", {"start": v(20.76, 190.9) * mm, "end": v(20.75, 206.35) * mm});
            skFitSpline(sketch, "E340.0", {"points": [v(173.58, -55.7) * mm, v(171.83, -49.34) * mm, v(170.1, -42.97) * mm, v(168.35, -36.6) * mm]});
            skFitSpline(sketch, "E341.0", {"points": [v(173.58, -143.92) * mm, v(173.58, -114.52) * mm, v(173.58, -85.11) * mm, v(173.58, -55.7) * mm]});
            skPoint(sketch, "E342", {"position": v(173.58, -55.7) * mm});
            skLineSegment(sketch, "E343", {"start": v(173.58, -55.7) * mm, "end": v(168.35, -36.6) * mm});
            skLineSegment(sketch, "E344", {"start": v(173.58, -55.7) * mm, "end": v(173.58, -143.92) * mm});
            skFitSpline(sketch, "E345.0", {"points": [v(173.5, -239.2) * mm, v(173.52, -234.94) * mm, v(173.55, -230.68) * mm, v(173.58, -226.42) * mm]});
            skFitSpline(sketch, "E346.0", {"points": [v(173.58, -226.42) * mm, v(173.58, -198.92) * mm, v(173.58, -171.42) * mm, v(173.58, -143.92) * mm]});
            skPoint(sketch, "E347", {"position": v(173.58, -226.42) * mm});
            skLineSegment(sketch, "E348", {"start": v(173.58, -226.42) * mm, "end": v(173.58, -143.92) * mm});
            skLineSegment(sketch, "E349", {"start": v(173.34, -242.62) * mm, "end": v(175.65, -259.5) * mm});
            skLineSegment(sketch, "E350", {"start": v(175.65, -259.5) * mm, "end": v(190.57, -284.2) * mm});
            skFitSpline(sketch, "E351.0", {"points": [v(173.4, -240.9) * mm, v(173.43, -240.33) * mm, v(173.46, -239.76) * mm, v(173.5, -239.2) * mm]});
            skFitSpline(sketch, "E352.0", {"points": [v(173.34, -242.62) * mm, v(173.36, -242.04) * mm, v(173.38, -241.47) * mm, v(173.4, -240.9) * mm]});
            skPoint(sketch, "E353", {"position": v(173.4, -240.9) * mm});
            skPoint(sketch, "E354", {"position": v(173.34, -242.62) * mm});
            skLineSegment(sketch, "E355", {"start": v(173.5, -239.2) * mm, "end": v(173.4, -240.9) * mm});
            skLineSegment(sketch, "E356", {"start": v(173.4, -240.9) * mm, "end": v(173.34, -242.62) * mm});
            skFitSpline(sketch, "E357.0", {"points": [v(268.7, 209) * mm, v(260.17, 204.5) * mm, v(251.64, 199.99) * mm, v(243.1, 195.48) * mm]});
            skFitSpline(sketch, "E358.0", {"points": [v(284.3, 233.23) * mm, v(279.1, 225.16) * mm, v(273.9, 217.08) * mm, v(268.7, 209) * mm]});
            skFitSpline(sketch, "E359.0", {"points": [v(243.1, 195.48) * mm, v(238.67, 194.99) * mm, v(234.24, 194.5) * mm, v(229.8, 194.01) * mm]});
            skFitSpline(sketch, "E360.0", {"points": [v(229.8, 194.01) * mm, v(229.56, 194.02) * mm, v(229.32, 194.02) * mm, v(229.08, 194.03) * mm]});
            skFitSpline(sketch, "E361.0", {"points": [v(229.08, 194.03) * mm, v(228.84, 194.03) * mm, v(228.6, 194.04) * mm, v(228.36, 194.05) * mm]});
            skPoint(sketch, "E362", {"position": v(228.36, 194.05) * mm});
            skPoint(sketch, "E363", {"position": v(229.08, 194.03) * mm});
            skPoint(sketch, "E364", {"position": v(229.8, 194.01) * mm});
            skLineSegment(sketch, "E365", {"start": v(228.36, 194.05) * mm, "end": v(229.08, 194.03) * mm});
            skLineSegment(sketch, "E366", {"start": v(229.08, 194.03) * mm, "end": v(229.8, 194.01) * mm});
            skLineSegment(sketch, "E367", {"start": v(229.8, 194.01) * mm, "end": v(243.1, 195.48) * mm});
            skLineSegment(sketch, "E368", {"start": v(243.1, 195.48) * mm, "end": v(268.7, 209) * mm});
            skLineSegment(sketch, "E369", {"start": v(268.7, 209) * mm, "end": v(284.3, 233.23) * mm});
            skFitSpline(sketch, "E370.0", {"points": [v(272.47, 288.98) * mm, v(276.9, 280.4) * mm, v(281.33, 271.82) * mm, v(285.76, 263.24) * mm]});
            skFitSpline(sketch, "E371.0", {"points": [v(248.4, 304.8) * mm, v(256.43, 299.53) * mm, v(264.45, 294.26) * mm, v(272.47, 288.98) * mm]});
            skFitSpline(sketch, "E372.0", {"points": [v(218.41, 306.55) * mm, v(228.41, 305.97) * mm, v(238.4, 305.39) * mm, v(248.4, 304.8) * mm]});
            skFitSpline(sketch, "E373.0", {"points": [v(192.53, 293.5) * mm, v(201.16, 297.85) * mm, v(209.79, 302.2) * mm, v(218.41, 306.55) * mm]});
            skPoint(sketch, "E374", {"position": v(218.41, 306.55) * mm});
            skPoint(sketch, "E375", {"position": v(248.4, 304.8) * mm});
            skPoint(sketch, "E376", {"position": v(272.47, 288.98) * mm});
            skLineSegment(sketch, "E377", {"start": v(285.76, 263.24) * mm, "end": v(272.47, 288.98) * mm});
            skLineSegment(sketch, "E378", {"start": v(272.47, 288.98) * mm, "end": v(248.4, 304.8) * mm});
            skLineSegment(sketch, "E379", {"start": v(248.4, 304.8) * mm, "end": v(218.41, 306.55) * mm});
            skLineSegment(sketch, "E380", {"start": v(218.41, 306.55) * mm, "end": v(192.53, 293.5) * mm});
            skLineSegment(sketch, "E381", {"start": v(285.76, 263.24) * mm, "end": v(284.3, 233.23) * mm});
            skFitSpline(sketch, "E382.0", {"points": [v(176.48, 269.6) * mm, v(181.83, 277.57) * mm, v(187.18, 285.54) * mm, v(192.53, 293.5) * mm]});
            skFitSpline(sketch, "E383.0", {"points": [v(173.34, 250.25) * mm, v(174.39, 256.7) * mm, v(175.44, 263.15) * mm, v(176.48, 269.6) * mm]});
            skLineSegment(sketch, "E384", {"start": v(192.53, 293.5) * mm, "end": v(176.48, 269.6) * mm});
            skLineSegment(sketch, "E385", {"start": v(176.48, 269.6) * mm, "end": v(173.34, 250.25) * mm});
            skFitSpline(sketch, "E386.0", {"points": [v(173.58, 47.42) * mm, v(173.54, 113.89) * mm, v(173.51, 180.36) * mm, v(173.48, 246.83) * mm]});
            skFitSpline(sketch, "E387.0", {"points": [v(169.6, 19.14) * mm, v(170.92, 28.57) * mm, v(172.25, 38) * mm, v(173.58, 47.42) * mm]});
            skLineSegment(sketch, "E388", {"start": v(173.58, 47.42) * mm, "end": v(169.6, 19.14) * mm});
            skLineSegment(sketch, "E389", {"start": v(173.58, 47.42) * mm, "end": v(173.48, 246.83) * mm});
            skLineSegment(sketch, "E390", {"start": v(173.48, 246.83) * mm, "end": v(173.34, 250.25) * mm});
            skFitSpline(sketch, "E391.0", {"points": [v(228.36, 194.05) * mm, v(228.26, 75.2) * mm, v(228.15, -43.63) * mm, v(228.04, -162.47) * mm]});
            skLineSegment(sketch, "E392", {"start": v(228.04, -162.47) * mm, "end": v(228.43, -186.57) * mm});
            skLineSegment(sketch, "E393", {"start": v(228.04, -162.47) * mm, "end": v(228.36, 194.05) * mm});
            skLineSegment(sketch, "E394", {"start": v(-208.32, -203.3) * mm, "end": v(-208.58, -247.43) * mm});
            skLineSegment(sketch, "E395", {"start": v(-263.99, 194.03) * mm, "end": v(-265.29, -186.54) * mm});
            skLineSegment(sketch, "E396", {"start": v(285.1, -258.45) * mm, "end": v(271.3, -283.77) * mm});
            skLineSegment(sketch, "E397", {"start": v(271.3, -283.77) * mm, "end": v(245.78, -298.15) * mm});
            skLineSegment(sketch, "E398", {"start": v(-208.45, 252.05) * mm, "end": v(-208.32, 250.9) * mm});
            skSolve(sketch);
        }
        {
            var Q0;
            Q0=makeQuery(id+"F0.imprint","IMPRINT",FACE,{"disambiguationData":[TD([[makeQuery(id+"F0.imprint","IMPRINT",EDGE,{"derivedFrom":sQuery(id+"F0.wireOp",EDGE,"E0.0")}),1.0]])]});
            extrude(context, id + "F1", {"entities" : qUnion([Q0]), "depth" : 63.5 * mm, "offsetDistance" : 25.4 * mm});
        }
        {
            var Q0;
            Q0=makeQuery(id+"F1.opExtrude","CAP_FACE",FACE,{"disambiguationData":[OSD([sQuery(id+"F0.wireOp",EDGE,"E0.0"),sQuery(id+"F0.wireOp",EDGE,"E1.0"),sQuery(id+"F0.wireOp",EDGE,"E2.0"),sQuery(id+"F0.wireOp",EDGE,"E7.0"),sQuery(id+"F0.wireOp",EDGE,"E8.0"),sQuery(id+"F0.wireOp",EDGE,"E10.0"),sQuery(id+"F0.wireOp",EDGE,"E12.0"),sQuery(id+"F0.wireOp",EDGE,"E15.0"),sQuery(id+"F0.wireOp",EDGE,"E16.0"),sQuery(id+"F0.wireOp",EDGE,"E30"),sQuery(id+"F0.wireOp",EDGE,"E31"),sQuery(id+"F0.wireOp",EDGE,"E32"),sQuery(id+"F0.wireOp",EDGE,"E33"),sQuery(id+"F0.wireOp",EDGE,"E34"),sQuery(id+"F0.wireOp",EDGE,"E35"),sQuery(id+"F0.wireOp",EDGE,"E36"),sQuery(id+"F0.wireOp",EDGE,"E43.0"),sQuery(id+"F0.wireOp",EDGE,"E45"),sQuery(id+"F0.wireOp",EDGE,"E46"),sQuery(id+"F0.wireOp",EDGE,"E47"),sQuery(id+"F0.wireOp",EDGE,"E48"),sQuery(id+"F0.wireOp",EDGE,"E54"),sQuery(id+"F0.wireOp",EDGE,"E55"),sQuery(id+"F0.wireOp",EDGE,"E64.0.2"),sQuery(id+"F0.wireOp",EDGE,"E65.0.1"),sQuery(id+"F0.wireOp",EDGE,"E68"),sQuery(id+"F0.wireOp",EDGE,"E69"),sQuery(id+"F0.wireOp",EDGE,"E70"),sQuery(id+"F0.wireOp",EDGE,"E71.0"),sQuery(id+"F0.wireOp",EDGE,"E74.0"),sQuery(id+"F0.wireOp",EDGE,"E79"),sQuery(id+"F0.wireOp",EDGE,"E81"),sQuery(id+"F0.wireOp",EDGE,"E83.0"),sQuery(id+"F0.wireOp",EDGE,"E86.0"),sQuery(id+"F0.wireOp",EDGE,"E87.0"),sQuery(id+"F0.wireOp",EDGE,"E93"),sQuery(id+"F0.wireOp",EDGE,"E94"),sQuery(id+"F0.wireOp",EDGE,"E95"),sQuery(id+"F0.wireOp",EDGE,"E96"),sQuery(id+"F0.wireOp",EDGE,"E100"),sQuery(id+"F0.wireOp",EDGE,"E101"),sQuery(id+"F0.wireOp",EDGE,"E120"),sQuery(id+"F0.wireOp",EDGE,"E121"),sQuery(id+"F0.wireOp",EDGE,"E122"),sQuery(id+"F0.wireOp",EDGE,"E123"),sQuery(id+"F0.wireOp",EDGE,"E124"),sQuery(id+"F0.wireOp",EDGE,"E125"),sQuery(id+"F0.wireOp",EDGE,"E126"),sQuery(id+"F0.wireOp",EDGE,"E127"),sQuery(id+"F0.wireOp",EDGE,"E128"),sQuery(id+"F0.wireOp",EDGE,"E129.0"),sQuery(id+"F0.wireOp",EDGE,"E130.0"),sQuery(id+"F0.wireOp",EDGE,"E131.0"),sQuery(id+"F0.wireOp",EDGE,"E136.0"),sQuery(id+"F0.wireOp",EDGE,"E137.0"),sQuery(id+"F0.wireOp",EDGE,"E140.0"),sQuery(id+"F0.wireOp",EDGE,"E141.0"),sQuery(id+"F0.wireOp",EDGE,"E142.0"),sQuery(id+"F0.wireOp",EDGE,"E143.0"),sQuery(id+"F0.wireOp",EDGE,"E144.0"),sQuery(id+"F0.wireOp",EDGE,"E151.0"),sQuery(id+"F0.wireOp",EDGE,"E154"),sQuery(id+"F0.wireOp",EDGE,"E157.0"),sQuery(id+"F0.wireOp",EDGE,"E158.0"),sQuery(id+"F0.wireOp",EDGE,"E160"),sQuery(id+"F0.wireOp",EDGE,"E161"),sQuery(id+"F0.wireOp",EDGE,"E162"),sQuery(id+"F0.wireOp",EDGE,"E165"),sQuery(id+"F0.wireOp",EDGE,"E166"),sQuery(id+"F0.wireOp",EDGE,"E169"),sQuery(id+"F0.wireOp",EDGE,"E170"),sQuery(id+"F0.wireOp",EDGE,"E181"),sQuery(id+"F0.wireOp",EDGE,"E182"),sQuery(id+"F0.wireOp",EDGE,"E183"),sQuery(id+"F0.wireOp",EDGE,"E184"),sQuery(id+"F0.wireOp",EDGE,"E185"),sQuery(id+"F0.wireOp",EDGE,"E192"),sQuery(id+"F0.wireOp",EDGE,"E193"),sQuery(id+"F0.wireOp",EDGE,"E194"),sQuery(id+"F0.wireOp",EDGE,"E201"),sQuery(id+"F0.wireOp",EDGE,"E202"),sQuery(id+"F0.wireOp",EDGE,"E203"),sQuery(id+"F0.wireOp",EDGE,"E205.0"),sQuery(id+"F0.wireOp",EDGE,"E204"),sQuery(id+"F0.wireOp",EDGE,"E221"),sQuery(id+"F0.wireOp",EDGE,"E222"),sQuery(id+"F0.wireOp",EDGE,"E223"),sQuery(id+"F0.wireOp",EDGE,"E224"),sQuery(id+"F0.wireOp",EDGE,"E225"),sQuery(id+"F0.wireOp",EDGE,"E226"),sQuery(id+"F0.wireOp",EDGE,"E230"),sQuery(id+"F0.wireOp",EDGE,"E231"),sQuery(id+"F0.wireOp",EDGE,"E233.0"),sQuery(id+"F0.wireOp",EDGE,"E234.0"),sQuery(id+"F0.wireOp",EDGE,"E236.0"),sQuery(id+"F0.wireOp",EDGE,"E237.0"),sQuery(id+"F0.wireOp",EDGE,"E238.0"),sQuery(id+"F0.wireOp",EDGE,"E239.0"),sQuery(id+"F0.wireOp",EDGE,"E244"),sQuery(id+"F0.wireOp",EDGE,"E246"),sQuery(id+"F0.wireOp",EDGE,"E251.0"),sQuery(id+"F0.wireOp",EDGE,"E256"),sQuery(id+"F0.wireOp",EDGE,"E264"),sQuery(id+"F0.wireOp",EDGE,"E265"),sQuery(id+"F0.wireOp",EDGE,"E266"),sQuery(id+"F0.wireOp",EDGE,"E255"),sQuery(id+"F0.wireOp",EDGE,"E267"),sQuery(id+"F0.wireOp",EDGE,"E270"),sQuery(id+"F0.wireOp",EDGE,"E271.0"),sQuery(id+"F0.wireOp",EDGE,"E273"),sQuery(id+"F0.wireOp",EDGE,"E279"),sQuery(id+"F0.wireOp",EDGE,"E280"),sQuery(id+"F0.wireOp",EDGE,"E281"),sQuery(id+"F0.wireOp",EDGE,"E285"),sQuery(id+"F0.wireOp",EDGE,"E286.0"),sQuery(id+"F0.wireOp",EDGE,"E288"),sQuery(id+"F0.wireOp",EDGE,"E289.0"),sQuery(id+"F0.wireOp",EDGE,"E296"),sQuery(id+"F0.wireOp",EDGE,"E297"),sQuery(id+"F0.wireOp",EDGE,"E302.0"),sQuery(id+"F0.wireOp",EDGE,"E300"),sQuery(id+"F0.wireOp",EDGE,"E306"),sQuery(id+"F0.wireOp",EDGE,"E298"),sQuery(id+"F0.wireOp",EDGE,"E310"),sQuery(id+"F0.wireOp",EDGE,"E311"),sQuery(id+"F0.wireOp",EDGE,"E314.0"),sQuery(id+"F0.wireOp",EDGE,"E312"),sQuery(id+"F0.wireOp",EDGE,"E318"),sQuery(id+"F0.wireOp",EDGE,"E321.0"),sQuery(id+"F0.wireOp",EDGE,"E322.0"),sQuery(id+"F0.wireOp",EDGE,"E324.0"),sQuery(id+"F0.wireOp",EDGE,"E327.0"),sQuery(id+"F0.wireOp",EDGE,"E333"),sQuery(id+"F0.wireOp",EDGE,"E334"),sQuery(id+"F0.wireOp",EDGE,"E335"),sQuery(id+"F0.wireOp",EDGE,"E338"),sQuery(id+"F0.wireOp",EDGE,"E339"),sQuery(id+"F0.wireOp",EDGE,"E343"),sQuery(id+"F0.wireOp",EDGE,"E344"),sQuery(id+"F0.wireOp",EDGE,"E345.0"),sQuery(id+"F0.wireOp",EDGE,"E348"),sQuery(id+"F0.wireOp",EDGE,"E349"),sQuery(id+"F0.wireOp",EDGE,"E350"),sQuery(id+"F0.wireOp",EDGE,"E355"),sQuery(id+"F0.wireOp",EDGE,"E356"),sQuery(id+"F0.wireOp",EDGE,"E365"),sQuery(id+"F0.wireOp",EDGE,"E366"),sQuery(id+"F0.wireOp",EDGE,"E367"),sQuery(id+"F0.wireOp",EDGE,"E368"),sQuery(id+"F0.wireOp",EDGE,"E369"),sQuery(id+"F0.wireOp",EDGE,"E377"),sQuery(id+"F0.wireOp",EDGE,"E378"),sQuery(id+"F0.wireOp",EDGE,"E379"),sQuery(id+"F0.wireOp",EDGE,"E380"),sQuery(id+"F0.wireOp",EDGE,"E381"),sQuery(id+"F0.wireOp",EDGE,"E384"),sQuery(id+"F0.wireOp",EDGE,"E385"),sQuery(id+"F0.wireOp",EDGE,"E388"),sQuery(id+"F0.wireOp",EDGE,"E389"),sQuery(id+"F0.wireOp",EDGE,"E390"),sQuery(id+"F0.wireOp",EDGE,"E392"),sQuery(id+"F0.wireOp",EDGE,"E393"),sQuery(id+"F0.wireOp",EDGE,"E394"),sQuery(id+"F0.wireOp",EDGE,"E395"),sQuery(id+"F0.wireOp",EDGE,"E396"),sQuery(id+"F0.wireOp",EDGE,"E397"),sQuery(id+"F0.wireOp",EDGE,"E398")])],"isStart":true});
            var sketch = newSketch(context, id + "F2", { "sketchPlane" : qUnion([Q0])});
            skLineSegment(sketch, "E399", {"start": v(-354.65, 304.9) * mm, "end": v(-354.65, 211.87) * mm, "construction": true});
            skLineSegment(sketch, "E400", {"start": v(-354.65, 388.54) * mm, "end": v(-354.65, 466.81) * mm, "construction": true});
            skLineSegment(sketch, "E401", {"start": v(388.3, 308.67) * mm, "end": v(388.3, 187.81) * mm, "construction": true});
            skLineSegment(sketch, "E402", {"start": v(223.7, 388.54) * mm, "end": v(303.14, 388.54) * mm, "construction": true});
            skLineSegment(sketch, "E403", {"start": v(-316.75, -350.17) * mm, "end": v(350.52, -350.17) * mm, "construction": true});
            skLineSegment(sketch, "E404", {"start": v(350.52, -350.17) * mm, "end": v(-316.75, -350.17) * mm, "construction": true});
            skLineSegment(sketch, "E405.bottom", {"start": v(-266.41, 388.54) * mm, "end": v(-171.2, 388.54) * mm, "construction": true});
            skLineSegment(sketch, "E406", {"start": v(16.83, 388.54) * mm, "end": v(16.83, -414.88) * mm, "construction": true});
            skLineSegment(sketch, "E407", {"start": v(-354.65, 19.18) * mm, "end": v(463.5, 19.18) * mm, "construction": true});
            skLineSegment(sketch, "E408.bottom", {"start": v(-266.41, 388.54) * mm, "end": v(-171.2, 388.54) * mm});
            skLineSegment(sketch, "E408.top", {"start": v(-316.75, -350.17) * mm, "end": v(350.52, -350.17) * mm});
            skLineSegment(sketch, "E408.left", {"start": v(-354.65, 304.9) * mm, "end": v(-354.65, 211.87) * mm});
            skLineSegment(sketch, "E408.right", {"start": v(388.3, 308.67) * mm, "end": v(388.3, 187.81) * mm});
            skLineSegment(sketch, "E409.0", {"start": v(-331.9, 335.96) * mm, "end": v(-266.41, 388.54) * mm});
            skLineSegment(sketch, "E410.0", {"start": v(-354.65, 304.9) * mm, "end": v(-331.9, 335.96) * mm});
            skFitSpline(sketch, "E411.0", {"points": [v(-171.2, 388.54) * mm, v(-160.11, 375.45) * mm, v(-149.02, 362.36) * mm, v(-137.92, 349.27) * mm]});
            skFitSpline(sketch, "E412.0", {"points": [v(-137.92, 349.27) * mm, v(-32.64, 349.27) * mm, v(72.64, 349.27) * mm, v(177.92, 349.27) * mm]});
            skFitSpline(sketch, "E413.0", {"points": [v(177.92, 349.27) * mm, v(193.18, 362.36) * mm, v(208.44, 375.45) * mm, v(223.7, 388.54) * mm]});
            skFitSpline(sketch, "E414.0", {"points": [v(303.14, 388.54) * mm, v(320.17, 376.06) * mm, v(337.2, 363.58) * mm, v(354.23, 351.1) * mm]});
            skFitSpline(sketch, "E415.0", {"points": [v(354.23, 351.1) * mm, v(365.59, 336.95) * mm, v(376.95, 322.8) * mm, v(388.3, 308.67) * mm]});
            skPoint(sketch, "E416.orphan", {"position": v(388.3, 388.54) * mm});
            skLineSegment(sketch, "E417.trimOffspring", {"start": v(-354.65, 388.54) * mm, "end": v(-512.24, 388.54) * mm, "construction": true});
            skLineSegment(sketch, "E418.trimOffspring", {"start": v(-171.2, 388.54) * mm, "end": v(-266.41, 388.54) * mm, "construction": true});
            skLineSegment(sketch, "E419.trimOffspring", {"start": v(223.7, 388.54) * mm, "end": v(303.14, 388.54) * mm});
            skLineSegment(sketch, "E420.trimOffspring", {"start": v(388.3, 388.54) * mm, "end": v(488.82, 388.54) * mm, "construction": true});
            skLineSegment(sketch, "E421.trimOffspring", {"start": v(388.3, 388.54) * mm, "end": v(388.3, 497.56) * mm, "construction": true});
            skLineSegment(sketch, "E422.0", {"start": v(-303.55, 164.27) * mm, "end": v(-354.65, 211.87) * mm});
            skFitSpline(sketch, "E423.0", {"points": [v(-303.55, -170.62) * mm, v(-303.55, -58.99) * mm, v(-303.55, 52.64) * mm, v(-303.55, 164.27) * mm]});
            skLineSegment(sketch, "E424.0", {"start": v(-303.55, -170.62) * mm, "end": v(-354.65, -200.14) * mm});
            skLineSegment(sketch, "E425.trimOffspring", {"start": v(-354.65, -200.14) * mm, "end": v(-354.65, -303.63) * mm, "construction": true});
            skLineSegment(sketch, "E426.trimOffspring", {"start": v(-354.65, -200.14) * mm, "end": v(-354.65, -303.63) * mm});
            skLineSegment(sketch, "E427.0", {"start": v(-355.44, -302.66) * mm, "end": v(-316.75, -350.17) * mm});
            skLineSegment(sketch, "E428.0", {"start": v(369.37, -335.03) * mm, "end": v(350.52, -350.17) * mm});
            skLineSegment(sketch, "E429.0", {"start": v(388.3, -309.2) * mm, "end": v(369.37, -335.03) * mm});
            skFitSpline(sketch, "E430.0", {"points": [v(353.14, -162.05) * mm, v(364.86, -170.48) * mm, v(376.58, -178.91) * mm, v(388.3, -187.34) * mm]});
            skLineSegment(sketch, "E431.0", {"start": v(353.14, 163.31) * mm, "end": v(353.14, -162.05) * mm});
            skPoint(sketch, "E432.0", {"position": v(388.3, 187.81) * mm});
            skLineSegment(sketch, "E433.trimOffspring", {"start": v(-354.65, -350.17) * mm, "end": v(-354.65, -441.1) * mm, "construction": true});
            skPoint(sketch, "E434.orphan", {"position": v(-354.65, -350.17) * mm});
            skLineSegment(sketch, "E435.trimOffspring", {"start": v(-354.65, -350.17) * mm, "end": v(-475.17, -350.17) * mm, "construction": true});
            skLineSegment(sketch, "E436.trimOffspring", {"start": v(388.3, -350.17) * mm, "end": v(511.42, -350.17) * mm, "construction": true});
            skLineSegment(sketch, "E437.trimOffspring", {"start": v(388.3, -350.17) * mm, "end": v(388.3, -425.73) * mm, "construction": true});
            skLineSegment(sketch, "E438.trimOffspring", {"start": v(388.3, -187.34) * mm, "end": v(388.3, -309.2) * mm, "construction": true});
            skLineSegment(sketch, "E439.trimOffspring", {"start": v(388.3, 187.81) * mm, "end": v(388.3, 308.67) * mm, "construction": true});
            skSolve(sketch);
        }
        {
            var Q0;
            Q0 = qSketchRegion(id + "F2", true);
            var Q1;
            Q1=makeQuery(id+"F0.imprint","IMPRINT",FACE,{"disambiguationData":[TD([[makeQuery(id+"F0.imprint","IMPRINT",EDGE,{"derivedFrom":sQuery(id+"F0.wireOp",EDGE,"E0.0")}),1.0]])]});
            var Q2;
            Q2=makeQuery(id+"F0.imprint","IMPRINT",FACE,{"disambiguationData":[TD([[makeQuery(id+"F0.imprint","IMPRINT",EDGE,{"derivedFrom":sQuery(id+"F0.wireOp",EDGE,"E64.0.2")}),-1.0]])]});
            extrude(context, id + "F3", {"entities" : qUnion([Q0, Q1, Q2]), "oppositeDirection" : true, "depth" : 5.08 * mm, "offsetDistance" : 25.4 * mm});
        }
    });
